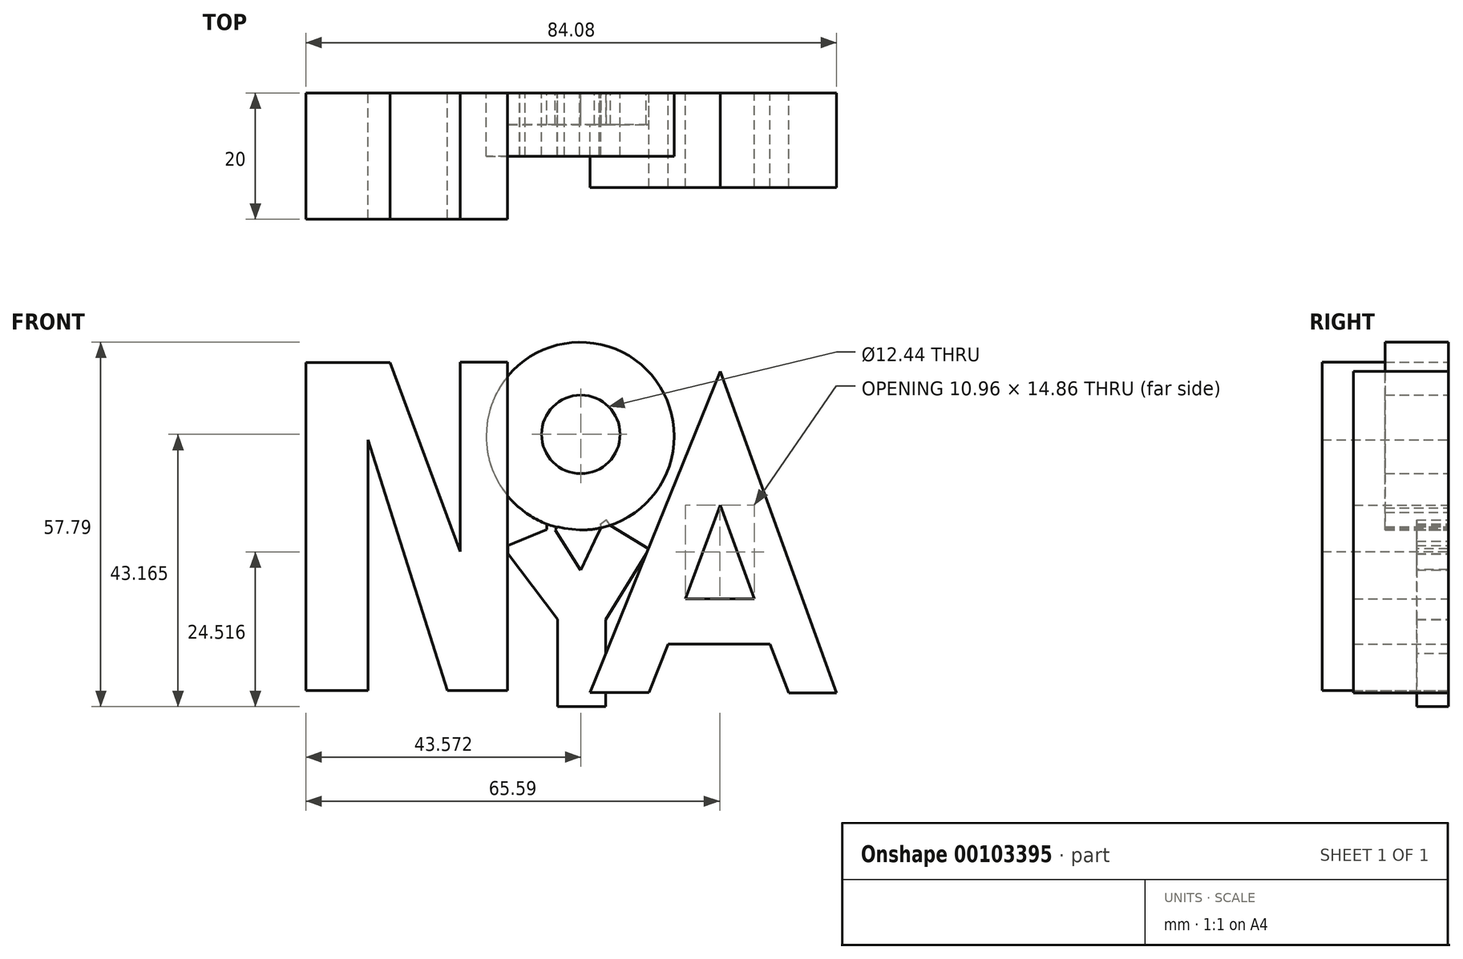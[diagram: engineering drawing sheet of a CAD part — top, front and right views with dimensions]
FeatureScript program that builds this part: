
annotation { "Feature Type Name" : "Feature", "Feature Type Description" : "" }
export const myFeature = defineFeature(function(context is Context, id is Id, definition is map)
    precondition{}
    {
        {
            var Q0;
            Q0=qCreatedBy(makeId("Front.planeOp"),FACE);
            var sketch = newSketch(context, id + "F0", { "sketchPlane" : qUnion([Q0])});
            skCircle(sketch, "E0", {"center": v(14.1, 12.16) * mm, "radius": 15 * mm});
            skPoint(sketch, "E1.end.orphan", {"position": v(12.56, -13.4) * mm});
            skPoint(sketch, "E1.start.orphan", {"position": v(2.53, -6.63) * mm});
            skPoint(sketch, "E2.end.orphan", {"position": v(22.89, 0) * mm});
            skPoint(sketch, "E3.end.orphan", {"position": v(24.91, -6.63) * mm});
            skPoint(sketch, "E4.end.orphan", {"position": v(21.1, -13.4) * mm});
            skPoint(sketch, "E5.end.orphan", {"position": v(5.33, 0) * mm});
            skLineSegment(sketch, "E6", {"start": v(8.79, -1.86) * mm, "end": v(2.53, -6.63) * mm});
            skLineSegment(sketch, "E7", {"start": v(2.53, -6.63) * mm, "end": v(10.52, -17.1) * mm});
            skLineSegment(sketch, "E8", {"start": v(10.52, -17.1) * mm, "end": v(10.52, -30.6) * mm});
            skLineSegment(sketch, "E9", {"start": v(10.52, -30.6) * mm, "end": v(18.1, -30.6) * mm});
            skLineSegment(sketch, "E10", {"start": v(18.1, -30.6) * mm, "end": v(18.1, -17.1) * mm});
            skLineSegment(sketch, "E11", {"start": v(18.1, -17.1) * mm, "end": v(24.91, -5.79) * mm});
            skLineSegment(sketch, "E12", {"start": v(24.91, -5.79) * mm, "end": v(18.91, -2.05) * mm});
            skLineSegment(sketch, "E13", {"start": v(18.91, -2.05) * mm, "end": v(14.16, -9.1) * mm});
            skLineSegment(sketch, "E14", {"start": v(14.16, -9.1) * mm, "end": v(8.79, -1.86) * mm});
            skLineSegment(sketch, "E15", {"start": v(36.28, 22.33) * mm, "end": v(16.02, -28.53) * mm});
            skLineSegment(sketch, "E16", {"start": v(36.28, 22.33) * mm, "end": v(54.68, -28.53) * mm});
            skLineSegment(sketch, "E17", {"start": v(54.68, -28.53) * mm, "end": v(47.03, -28.53) * mm});
            skLineSegment(sketch, "E18", {"start": v(47.03, -28.53) * mm, "end": v(36.28, 1.18) * mm});
            skLineSegment(sketch, "E19", {"start": v(36.28, 1.18) * mm, "end": v(25.12, -28.53) * mm});
            skLineSegment(sketch, "E20", {"start": v(25.12, -28.53) * mm, "end": v(16.02, -28.53) * mm});
            skLineSegment(sketch, "E21", {"start": v(30.7, -13.67) * mm, "end": v(41.66, -13.67) * mm});
            skLineSegment(sketch, "E22", {"start": v(28.05, -20.74) * mm, "end": v(44.22, -20.74) * mm});
            skLineSegment(sketch, "E23", {"start": v(2.53, 23.8) * mm, "end": v(2.53, -28.24) * mm});
            skLineSegment(sketch, "E24", {"start": v(2.53, -28.24) * mm, "end": v(-7.04, -28.24) * mm});
            skLineSegment(sketch, "E25", {"start": v(-7.04, -28.24) * mm, "end": v(-19.57, 11.54) * mm});
            skLineSegment(sketch, "E26", {"start": v(-19.57, 11.54) * mm, "end": v(-19.57, -28.24) * mm});
            skLineSegment(sketch, "E27", {"start": v(-19.57, -28.24) * mm, "end": v(-29.4, -28.24) * mm});
            skLineSegment(sketch, "E28", {"start": v(-29.4, -28.24) * mm, "end": v(-29.4, 23.8) * mm});
            skLineSegment(sketch, "E29", {"start": v(-29.4, 23.8) * mm, "end": v(-16, 23.8) * mm});
            skLineSegment(sketch, "E30", {"start": v(-16, 23.8) * mm, "end": v(-4.92, -6.27) * mm});
            skLineSegment(sketch, "E31", {"start": v(-4.92, -6.27) * mm, "end": v(-4.92, 23.8) * mm});
            skLineSegment(sketch, "E32", {"start": v(-4.92, 23.8) * mm, "end": v(2.53, 23.8) * mm});
            skLineSegment(sketch, "E33.bottom", {"start": v(23.34, -6.58) * mm, "end": v(27.06, -6.58) * mm});
            skLineSegment(sketch, "E33.top", {"start": v(23.34, -4.88) * mm, "end": v(27.06, -4.88) * mm});
            skLineSegment(sketch, "E33.left", {"start": v(23.34, -6.58) * mm, "end": v(23.34, -4.88) * mm});
            skLineSegment(sketch, "E33.right", {"start": v(27.06, -6.58) * mm, "end": v(27.06, -4.88) * mm});
            skSolve(sketch);
        }
        {
            var Q0;
            Q0=qCreatedBy(makeId("Front.planeOp"),FACE);
            var sketch = newSketch(context, id + "F1", { "sketchPlane" : qUnion([Q0])});
            skLineSegment(sketch, "E34", {"start": v(-29.4, -28.23) * mm, "end": v(-29.4, 23.79) * mm});
            skLineSegment(sketch, "E35", {"start": v(-29.4, 23.79) * mm, "end": v(-16.04, 23.79) * mm});
            skLineSegment(sketch, "E36", {"start": v(-16.04, 23.79) * mm, "end": v(-4.99, -6.19) * mm});
            skLineSegment(sketch, "E37", {"start": v(-4.99, -6.19) * mm, "end": v(-4.99, 23.88) * mm});
            skLineSegment(sketch, "E38", {"start": v(-4.99, 23.88) * mm, "end": v(2.55, 23.88) * mm});
            skLineSegment(sketch, "E39", {"start": v(2.55, 23.88) * mm, "end": v(2.55, -28.24) * mm});
            skLineSegment(sketch, "E40", {"start": v(2.55, -28.24) * mm, "end": v(-7.01, -28.24) * mm});
            skLineSegment(sketch, "E41", {"start": v(-7.01, -28.24) * mm, "end": v(-19.58, 11.56) * mm});
            skLineSegment(sketch, "E42", {"start": v(-19.58, 11.56) * mm, "end": v(-19.58, -28.24) * mm});
            skLineSegment(sketch, "E43", {"start": v(-19.58, -28.24) * mm, "end": v(-29.4, -28.23) * mm});
            skSolve(sketch);
        }
        {
            var Q0;
            Q0=qCreatedBy(makeId("Front.planeOp"),FACE);
            var sketch = newSketch(context, id + "F2", { "sketchPlane" : qUnion([Q0])});
            skCircle(sketch, "E44", {"center": v(14.06, 12.13) * mm, "radius": 14.9 * mm});
            skSolve(sketch);
        }
        {
            var Q0;
            Q0=qCreatedBy(makeId("Front.planeOp"),FACE);
            var sketch = newSketch(context, id + "F3", { "sketchPlane" : qUnion([Q0])});
            skLineSegment(sketch, "E45", {"start": v(8.75, -1.77) * mm, "end": v(8.75, -2.69) * mm});
            skLineSegment(sketch, "E46", {"start": v(8.75, -2.69) * mm, "end": v(2.6, -5.2) * mm});
            skLineSegment(sketch, "E47", {"start": v(2.6, -5.2) * mm, "end": v(2.6, -6.5) * mm});
            skLineSegment(sketch, "E48", {"start": v(2.6, -6.5) * mm, "end": v(10.45, -16.88) * mm});
            skLineSegment(sketch, "E49", {"start": v(10.45, -16.88) * mm, "end": v(10.45, -30.76) * mm});
            skLineSegment(sketch, "E50", {"start": v(10.45, -30.76) * mm, "end": v(18.13, -30.76) * mm});
            skLineSegment(sketch, "E51", {"start": v(18.13, -30.76) * mm, "end": v(18.13, -16.97) * mm});
            skLineSegment(sketch, "E52", {"start": v(18.13, -16.97) * mm, "end": v(25, -5.82) * mm});
            skLineSegment(sketch, "E53", {"start": v(25, -5.82) * mm, "end": v(18.85, -2.04) * mm});
            skLineSegment(sketch, "E54", {"start": v(18.85, -2.04) * mm, "end": v(18.25, -1.18) * mm});
            skLineSegment(sketch, "E55", {"start": v(18.25, -1.18) * mm, "end": v(17.19, -1.91) * mm});
            skLineSegment(sketch, "E56", {"start": v(17.19, -1.91) * mm, "end": v(17.41, -2.24) * mm});
            skLineSegment(sketch, "E57", {"start": v(17.41, -2.24) * mm, "end": v(14.1, -9.1) * mm});
            skLineSegment(sketch, "E58", {"start": v(14.1, -9.1) * mm, "end": v(10.11, -2.77) * mm});
            skLineSegment(sketch, "E59", {"start": v(10.11, -2.77) * mm, "end": v(10.52, -2.26) * mm});
            skLineSegment(sketch, "E60", {"start": v(10.52, -2.26) * mm, "end": v(8.75, -1.77) * mm});
            skSolve(sketch);
        }
        {
            var Q0;
            Q0=qCreatedBy(makeId("Front.planeOp"),FACE);
            var sketch = newSketch(context, id + "F4", { "sketchPlane" : qUnion([Q0])});
            skLineSegment(sketch, "E61", {"start": v(36.26, 22.4) * mm, "end": v(15.65, -28.51) * mm});
            skLineSegment(sketch, "E62", {"start": v(15.65, -28.51) * mm, "end": v(24.96, -28.51) * mm});
            skLineSegment(sketch, "E63", {"start": v(24.96, -28.51) * mm, "end": v(28.03, -20.86) * mm});
            skLineSegment(sketch, "E64", {"start": v(28.03, -20.86) * mm, "end": v(44.13, -20.86) * mm});
            skLineSegment(sketch, "E65", {"start": v(44.13, -20.86) * mm, "end": v(47.09, -28.59) * mm});
            skLineSegment(sketch, "E66", {"start": v(47.09, -28.59) * mm, "end": v(54.67, -28.59) * mm});
            skLineSegment(sketch, "E67", {"start": v(54.67, -28.59) * mm, "end": v(36.26, 22.4) * mm});
            skSolve(sketch);
        }
        {
            var Q0;
            Q0=qCreatedBy(makeId("Front.planeOp"),FACE);
            var sketch = newSketch(context, id + "F5", { "sketchPlane" : qUnion([Q0])});
            skCircle(sketch, "E68", {"center": v(14.16, 12.4) * mm, "radius": 6.22 * mm});
            skLineSegment(sketch, "E69", {"start": v(10.1, -2.72) * mm, "end": v(14.16, -9.1) * mm});
            skLineSegment(sketch, "E70", {"start": v(14.16, -9.1) * mm, "end": v(17.33, -2.35) * mm});
            skLineSegment(sketch, "E71", {"start": v(17.33, -2.35) * mm, "end": v(16.35, -2.79) * mm});
            skLineSegment(sketch, "E72", {"start": v(16.35, -2.79) * mm, "end": v(14.1, -2.79) * mm});
            skLineSegment(sketch, "E73", {"start": v(14.1, -2.79) * mm, "end": v(11.56, -2.52) * mm});
            skLineSegment(sketch, "E74", {"start": v(11.56, -2.52) * mm, "end": v(10.47, -2.25) * mm});
            skLineSegment(sketch, "E75", {"start": v(4.26, 0.78) * mm, "end": v(4.26, -4.42) * mm});
            skLineSegment(sketch, "E76", {"start": v(4.26, -4.42) * mm, "end": v(8.73, -2.63) * mm});
            skLineSegment(sketch, "E77", {"start": v(4.26, 0.78) * mm, "end": v(4.52, 0.73) * mm});
            skLineSegment(sketch, "E78", {"start": v(4.52, 0.73) * mm, "end": v(6.15, -0.64) * mm});
            skLineSegment(sketch, "E79", {"start": v(6.15, -0.64) * mm, "end": v(7.98, -1.61) * mm});
            skLineSegment(sketch, "E80", {"start": v(7.98, -1.61) * mm, "end": v(8.73, -1.8) * mm});
            skLineSegment(sketch, "E81", {"start": v(8.73, -1.8) * mm, "end": v(8.73, -2.63) * mm});
            skLineSegment(sketch, "E82", {"start": v(10.1, -2.72) * mm, "end": v(10.47, -2.25) * mm});
            skLineSegment(sketch, "E83", {"start": v(36.3, 1.21) * mm, "end": v(30.72, -13.7) * mm});
            skLineSegment(sketch, "E84", {"start": v(30.72, -13.7) * mm, "end": v(41.73, -13.7) * mm});
            skLineSegment(sketch, "E85", {"start": v(41.73, -13.7) * mm, "end": v(36.3, 1.21) * mm});
            skSolve(sketch);
        }
        {
            var Q0;
            Q0 = qSketchRegion(id + "F1", true);
            var Q1;
            Q1 = qConstructionFilter(qBodyType(qCreatedBy(id + "F1" ,EDGE), BodyType.WIRE), ConstructionObject.NO);
            extrude(context, id + "F6", {"entities" : qUnion([Q0]), "surfaceEntities" : qUnion([Q1]), "depth" : 20 * mm});
        }
        {
            var Q0;
            Q0 = qSketchRegion(id + "F3", true);
            extrude(context, id + "F7", {"entities" : qUnion([Q0]), "depth" : 5 * mm});
        }
        {
            var Q0;
            Q0 = qSketchRegion(id + "F2", true);
            extrude(context, id + "F8", {"entities" : qUnion([Q0]), "depth" : 10 * mm});
        }
        {
            var Q0;
            Q0 = qSketchRegion(id + "F4", true);
            extrude(context, id + "F9", {"entities" : qUnion([Q0]), "operationType" : NewBodyOperationType.ADD, "depth" : 15 * mm});
        }
        {
            var Q0;
            Q0=makeQuery(id+"F5.imprint","IMPRINT",FACE,{"disambiguationData":[TD([[makeQuery(id+"F5.imprint","IMPRINT",EDGE,{"derivedFrom":sQuery(id+"F5.wireOp",EDGE,"E69")}),1.0]])]});
            var Q1;
            Q1=makeQuery(id+"F5.imprint","IMPRINT",FACE,{"disambiguationData":[TD([[makeQuery(id+"F5.imprint","IMPRINT",EDGE,{"derivedFrom":sQuery(id+"F5.wireOp",EDGE,"E68")}),1.0]])]});
            var Q2;
            Q2=makeQuery(id+"F5.imprint","IMPRINT",FACE,{"disambiguationData":[TD([[makeQuery(id+"F5.imprint","IMPRINT",EDGE,{"derivedFrom":sQuery(id+"F5.wireOp",EDGE,"E75")}),1.0]])]});
            var Q3;
            {var subQ3=sQuery(id+"F0.wireOp",EDGE,"E21");Q3=makeQuery(id+"F0.imprint","IMPRINT",FACE,{"disambiguationData":[TD([[makeQuery(id+"F0.imprint","IMPRINT",EDGE,{"derivedFrom":subQ3}),1.0]])]});}
            extrude(context, id + "F10", {"entities" : qUnion([Q0, Q1, Q2, Q3]), "operationType" : NewBodyOperationType.REMOVE, "endBound" : BoundingType.THROUGH_ALL, "depth" : 25 * mm});
        }
    });
